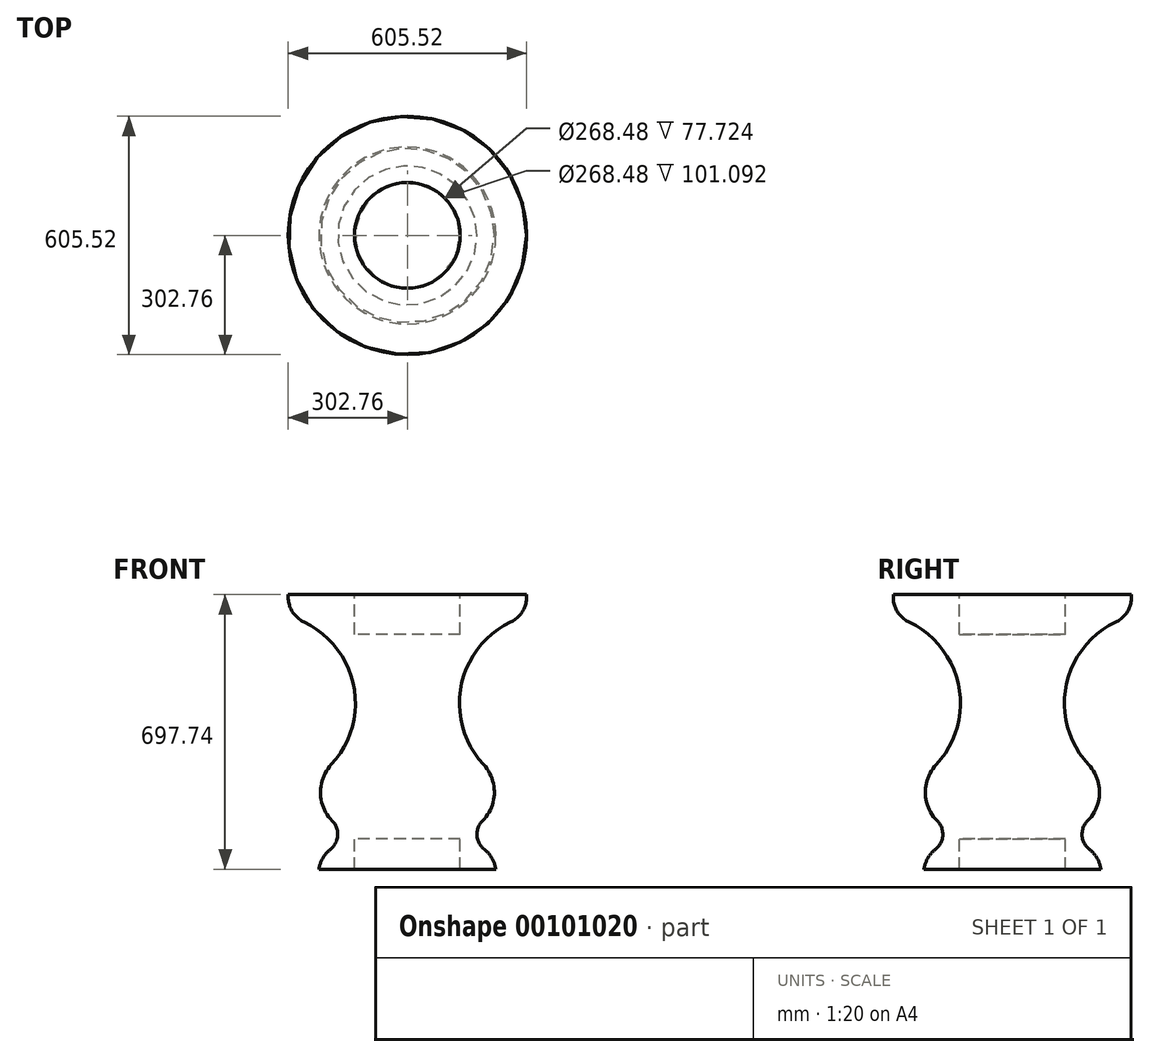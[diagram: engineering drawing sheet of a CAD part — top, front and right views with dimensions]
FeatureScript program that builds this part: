
annotation { "Feature Type Name" : "Feature", "Feature Type Description" : "" }
export const myFeature = defineFeature(function(context is Context, id is Id, definition is map)
    precondition{}
    {
        {
            var Q0;
            Q0=qCreatedBy(makeId("Front.planeOp"),FACE);
            var sketch = newSketch(context, id + "F0", { "sketchPlane" : qUnion([Q0])});
            skLineSegment(sketch, "E0", {"start": v(0, 0) * mm, "end": v(0, 166.62) * mm});
            skLineSegment(sketch, "E1", {"start": v(0, 166.62) * mm, "end": v(134.24, 166.62) * mm});
            skLineSegment(sketch, "E2", {"start": v(134.24, 166.62) * mm, "end": v(134.24, 267.72) * mm});
            skLineSegment(sketch, "E3", {"start": v(134.24, 267.72) * mm, "end": v(302.51, 267.72) * mm});
            skLineSegment(sketch, "E4", {"start": v(0, 0) * mm, "end": v(0, -352.3) * mm});
            skLineSegment(sketch, "E5", {"start": v(0, -352.3) * mm, "end": v(134.24, -352.3) * mm});
            skLineSegment(sketch, "E6", {"start": v(134.24, -352.3) * mm, "end": v(134.24, -430.02) * mm});
            skLineSegment(sketch, "E7", {"start": v(134.24, -430.02) * mm, "end": v(224.6, -430.02) * mm});
            skLineSegment(sketch, "E8", {"start": v(0, -430.02) * mm, "end": v(225.3, -430.02) * mm, "construction": true});
            skPoint(sketch, "E8.endSnap0", {"position": v(179.42, -430.02) * mm});
            skLineSegment(sketch, "E9", {"start": v(225.3, -430.02) * mm, "end": v(225.3, -341.12) * mm, "construction": true});
            skArc(sketch, "E10", {"start": v(190.96, -306.85) * mm, "mid": v(176.88, -344.16) * mm, "end": v(195.5, -379.4) * mm});
            skArc(sketch, "E11", {"start": v(224.6, -430.02) * mm, "mid": v(215.02, -401.86) * mm, "end": v(195.5, -379.4) * mm});
            skLineSegment(sketch, "E12", {"start": v(0, -430.02) * mm, "end": v(0, -234.19) * mm, "construction": true});
            skLineSegment(sketch, "E13", {"start": v(0, -234.19) * mm, "end": v(118.14, -234.19) * mm, "construction": true});
            skArc(sketch, "E14", {"start": v(190.96, -306.85) * mm, "mid": v(221, -235.94) * mm, "end": v(193.4, -164.05) * mm});
            skArc(sketch, "E15", {"start": v(262.33, 197.85) * mm, "mid": v(136.11, 34.38) * mm, "end": v(193.4, -164.05) * mm});
            skArc(sketch, "E16", {"start": v(262.33, 197.85) * mm, "mid": v(293.32, 226.52) * mm, "end": v(302.51, 267.72) * mm});
            skPoint(sketch, "E17.orphan", {"position": v(507.14, 166.62) * mm});
            skSolve(sketch);
        }
        {
            var Q0;
            Q0=makeQuery(id+"F0.imprint","IMPRINT",FACE,{"disambiguationData":[TD([[makeQuery(id+"F0.imprint","IMPRINT",EDGE,{"derivedFrom":sQuery(id+"F0.wireOp",EDGE,"E0")}),-1.0]])]});
            var Q1;
            Q1=sQuery(id+"F0.wireOp",EDGE,"E4");
            revolve(context, id + "F1", {"entities" : qUnion([Q0]), "axis" : qUnion([Q1]), "revolveType" : RevolveType.FULL});
        }
    });
